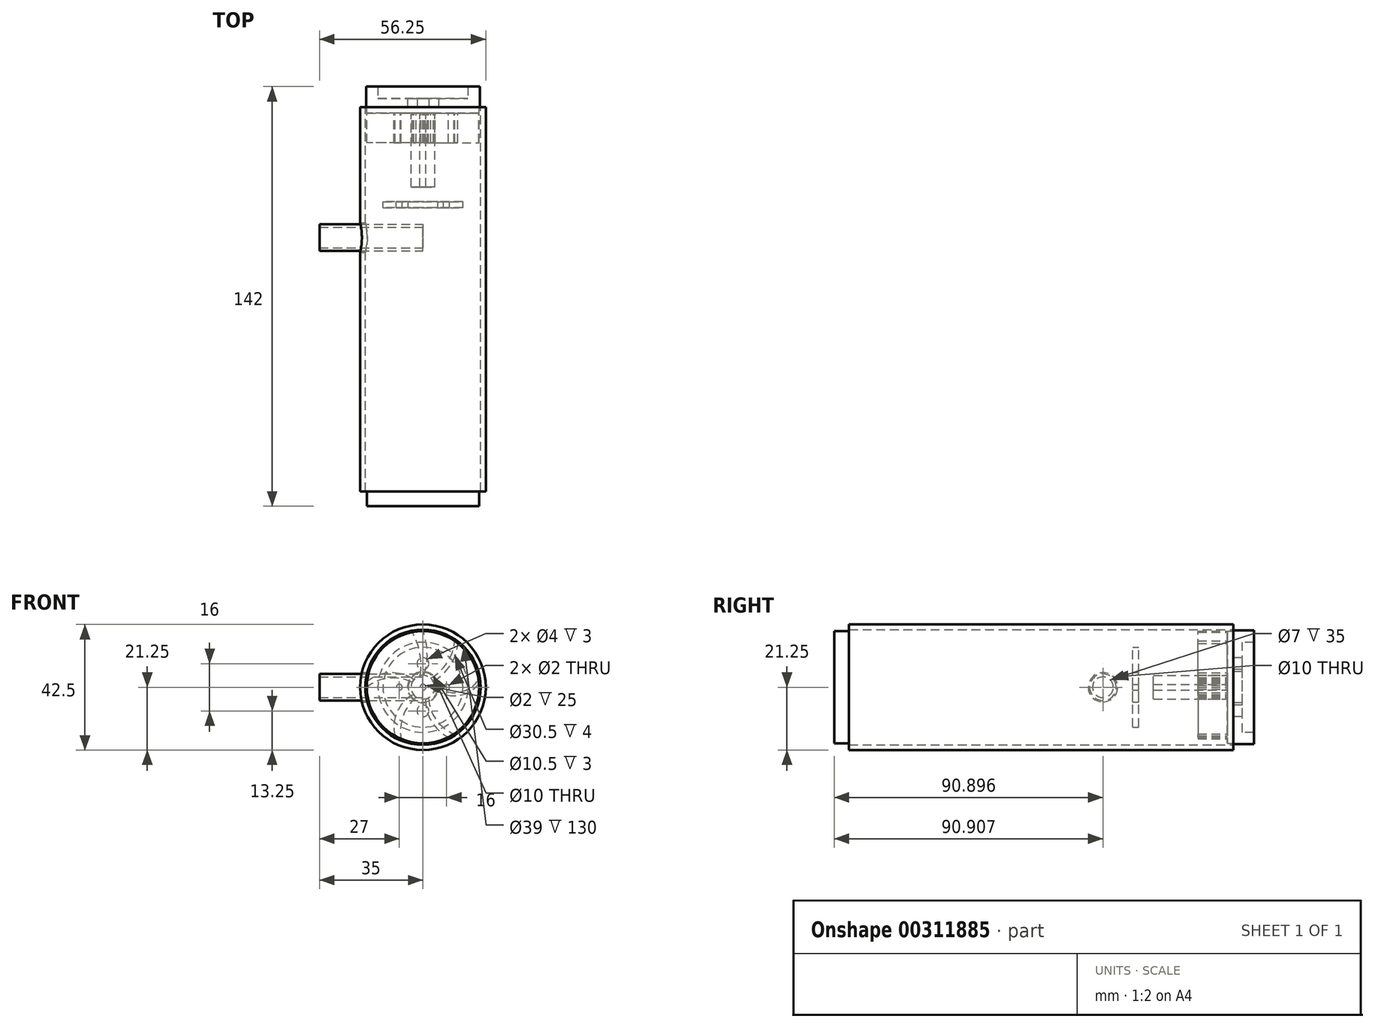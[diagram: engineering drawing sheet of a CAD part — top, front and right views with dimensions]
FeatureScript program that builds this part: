
annotation { "Feature Type Name" : "Feature", "Feature Type Description" : "" }
export const myFeature = defineFeature(function(context is Context, id is Id, definition is map)
    precondition{}
    {
        {
            var Q0;
            Q0=qCreatedBy(makeId("Front.planeOp"),FACE);
            var sketch = newSketch(context, id + "F0", { "sketchPlane" : qUnion([Q0])});
            skCircle(sketch, "E0", {"center": v(0, 0) * mm, "radius": 19.5 * mm});
            skCircle(sketch, "E1", {"center": v(0, 0) * mm, "radius": 21.25 * mm});
            skSolve(sketch);
        }
        {
            var Q0;
            Q0 = qSketchRegion(id + "F0", true);
            extrude(context, id + "F1", {"entities" : qUnion([Q0]), "depth" : 130 * mm});
        }
        {
            var Q0;
            Q0=qCreatedBy(makeId("Front.planeOp"),FACE);
            var sketch = newSketch(context, id + "F2", { "sketchPlane" : qUnion([Q0])});
            skCircle(sketch, "E2", {"center": v(0, 0) * mm, "radius": 19 * mm});
            skSolve(sketch);
        }
        {
            var Q0;
            Q0 = qSketchRegion(id + "F2", true);
            extrude(context, id + "F3", {"entities" : qUnion([Q0]), "depth" : 2 * mm});
        }
        {
            var Q0;
            Q0=makeQuery(id+"F3.opExtrude","CAP_FACE",FACE,{"disambiguationData":[OSD([sQuery(id+"F2.wireOp",EDGE,"E2")])],"isStart":false});
            var sketch = newSketch(context, id + "F4", { "sketchPlane" : qUnion([Q0])});
            skCircle(sketch, "E3", {"center": v(0, 0) * mm, "radius": 4.1 * mm});
            skArc(sketch, "E4", {"start": v(4.04, -0.63) * mm, "mid": v(11.9, -2.82) * mm, "end": v(18.96, 1.28) * mm});
            skArc(sketch, "E5", {"start": v(4.04, 0.63) * mm, "mid": v(11.86, -1.73) * mm, "end": v(18.83, 2.51) * mm});
            skArc(sketch, "E6", {"start": v(1.89, -3.63) * mm, "mid": v(4.47, -10.95) * mm, "end": v(10.5, -15.83) * mm});
            skArc(sketch, "E7", {"start": v(0.8, -4.02) * mm, "mid": v(2.9, -11.58) * mm, "end": v(8.66, -16.91) * mm});
            skArc(sketch, "E8", {"start": v(-3.11, 2.66) * mm, "mid": v(-11.15, 4.86) * mm, "end": v(-18.91, 1.83) * mm});
            skArc(sketch, "E9", {"start": v(-3.72, 1.7) * mm, "mid": v(-11.61, 3.1) * mm, "end": v(-19, 0) * mm});
            skArc(sketch, "E10", {"start": v(-3.24, -2.5) * mm, "mid": v(-8.8, -8.4) * mm, "end": v(-9.46, -16.48) * mm});
            skArc(sketch, "E11", {"start": v(-2.29, -3.4) * mm, "mid": v(-6.72, -9.76) * mm, "end": v(-7.43, -17.49) * mm});
            skArc(sketch, "E12", {"start": v(-0.88, 4) * mm, "mid": v(-1.03, 11.55) * mm, "end": v(-3.62, 18.65) * mm});
            skArc(sketch, "E13", {"start": v(0.36, 4.08) * mm, "mid": v(1.43, 11.57) * mm, "end": v(0, 19) * mm});
            skArc(sketch, "E14", {"start": v(2.63, 3.14) * mm, "mid": v(8.26, 8.38) * mm, "end": v(10.76, 15.66) * mm});
            skArc(sketch, "E15", {"start": v(3.5, 2.11) * mm, "mid": v(9.3, 7.43) * mm, "end": v(11.84, 14.86) * mm});
            skCircle(sketch, "E16", {"center": v(0, 0) * mm, "radius": 1 * mm});
            skSolve(sketch);
        }
        {
            var Q0;
            {var subQ0=sQuery(id+"F4.wireOp",EDGE,"E12");Q0=makeQuery(id+"F4.imprint","IMPRINT",FACE,{"disambiguationData":[TD([[makeQuery(id+"F4.imprint","IMPRINT",EDGE,{"derivedFrom":subQ0}),-1.0]])]});}
            var Q1;
            {var subQ0=sQuery(id+"F4.wireOp",EDGE,"E4");Q1=makeQuery(id+"F4.imprint","IMPRINT",FACE,{"disambiguationData":[TD([[makeQuery(id+"F4.imprint","IMPRINT",EDGE,{"derivedFrom":subQ0}),1.0]])]});}
            var Q2;
            {var subQ0=sQuery(id+"F4.wireOp",EDGE,"E6");Q2=makeQuery(id+"F4.imprint","IMPRINT",FACE,{"disambiguationData":[TD([[makeQuery(id+"F4.imprint","IMPRINT",EDGE,{"derivedFrom":subQ0}),-1.0]])]});}
            var Q3;
            {var subQ0=sQuery(id+"F4.wireOp",EDGE,"E10");Q3=makeQuery(id+"F4.imprint","IMPRINT",FACE,{"disambiguationData":[TD([[makeQuery(id+"F4.imprint","IMPRINT",EDGE,{"derivedFrom":subQ0}),1.0]])]});}
            var Q4;
            {var subQ0=sQuery(id+"F4.wireOp",EDGE,"E14");Q4=makeQuery(id+"F4.imprint","IMPRINT",FACE,{"disambiguationData":[TD([[makeQuery(id+"F4.imprint","IMPRINT",EDGE,{"derivedFrom":subQ0}),-1.0]])]});}
            var Q5;
            {var subQ0=sQuery(id+"F4.wireOp",EDGE,"E8");Q5=makeQuery(id+"F4.imprint","IMPRINT",FACE,{"disambiguationData":[TD([[makeQuery(id+"F4.imprint","IMPRINT",EDGE,{"derivedFrom":subQ0}),1.0]])]});}
            extrude(context, id + "F5", {"entities" : qUnion([Q0, Q1, Q2, Q3, Q4, Q5]), "operationType" : NewBodyOperationType.ADD, "depth" : 10 * mm});
        }
        {
            var Q0;
            {var subQ0=sQuery(id+"F4.wireOp",EDGE,"E8");var subQ1=makeQuery(id+"F3.opExtrude","CAP_EDGE",EDGE,{"disambiguationData":[OSD([sQuery(id+"F2.wireOp",EDGE,"E2")])],"isStart":false});var subQ2=makeQuery(id+"F4.imprint","INTERSECT",VERTEX,{"derivedFrom":[subQ1,subQ0]});Q0=makeQuery(id+"F4.imprint","IMPRINT",FACE,{"disambiguationData":[TD([[makeQuery(id+"F4.imprint","IMPRINT",EDGE,{"disambiguationData":[TD([[subQ2,1.0]])],"derivedFrom":subQ0}),-1.0]])]});}
            var sketch = newSketch(context, id + "F6", { "sketchPlane" : qUnion([Q0])});
            skCircle(sketch, "E17", {"center": v(0, 0) * mm, "radius": 4 * mm});
            skCircle(sketch, "E18", {"center": v(0, 0) * mm, "radius": 1 * mm});
            skSolve(sketch);
        }
        {
            var Q0;
            Q0 = qSketchRegion(id + "F6", true);
            extrude(context, id + "F7", {"entities" : qUnion([Q0]), "operationType" : NewBodyOperationType.ADD, "depth" : 25 * mm});
        }
        {
            var Q0;
            {var subQ0=sQuery(id+"F4.wireOp",EDGE,"E4");Q0=makeQuery(id+"F4.imprint","IMPRINT",FACE,{"disambiguationData":[TD([[makeQuery(id+"F4.imprint","IMPRINT",EDGE,{"derivedFrom":subQ0}),-1.0]])]});}
            cPlane(context, id + "F8", {"entities" : qUnion([Q0]), "cplaneType" : CPlaneType.OFFSET, "offset" : 30 * mm, "width" : 150 * mm, "height" : 150 * mm});
        }
        {
            var Q0;
            Q0=qCreatedBy(id+"F8.planeOp",FACE);
            var sketch = newSketch(context, id + "F9", { "sketchPlane" : qUnion([Q0])});
            skCircle(sketch, "E19", {"center": v(0, 0) * mm, "radius": 5 * mm});
            skCircle(sketch, "E20", {"center": v(0, 0) * mm, "radius": 13.5 * mm});
            skCircle(sketch, "E21", {"center": v(8, 0) * mm, "radius": 1 * mm});
            skCircle(sketch, "E22", {"center": v(-8, 0) * mm, "radius": 1 * mm});
            skSolve(sketch);
        }
        {
            var Q0;
            Q0=makeQuery(id+"F9.imprint","IMPRINT",FACE,{"disambiguationData":[TD([[makeQuery(id+"F9.imprint","IMPRINT",EDGE,{"derivedFrom":sQuery(id+"F9.wireOp",EDGE,"E19")}),-1.0]])]});
            extrude(context, id + "F10", {"entities" : qUnion([Q0]), "depth" : 2 * mm});
        }
        {
            var Q0;
            Q0=makeQuery(id+"F1.opExtrude","CAP_FACE",FACE,{"disambiguationData":[OSD([sQuery(id+"F0.wireOp",EDGE,"E0"),sQuery(id+"F0.wireOp",EDGE,"E1")])],"isStart":false});
            var sketch = newSketch(context, id + "F11", { "sketchPlane" : qUnion([Q0])});
            skCircle(sketch, "E23", {"center": v(0, 0) * mm, "radius": 19 * mm});
            skSolve(sketch);
        }
        {
            var Q0;
            Q0 = qSketchRegion(id + "F11", true);
            extrude(context, id + "F12", {"entities" : qUnion([Q0]), "depth" : 5 * mm});
        }
        {
            var Q0;
            Q0=qCreatedBy(makeId("Front.planeOp"),FACE);
            var sketch = newSketch(context, id + "F13", { "sketchPlane" : qUnion([Q0])});
            skCircle(sketch, "E24", {"center": v(0, 0) * mm, "radius": 19.25 * mm});
            skCircle(sketch, "E25", {"center": v(0, -8) * mm, "radius": 2 * mm});
            skCircle(sketch, "E26", {"center": v(0, 8) * mm, "radius": 2 * mm});
            skCircle(sketch, "E27", {"center": v(0, 0) * mm, "radius": 5.25 * mm});
            skSolve(sketch);
        }
        {
            var Q0;
            Q0=makeQuery(id+"F13.imprint","IMPRINT",FACE,{"disambiguationData":[TD([[makeQuery(id+"F13.imprint","IMPRINT",EDGE,{"derivedFrom":sQuery(id+"F13.wireOp",EDGE,"E24")}),1.0]])]});
            var sketch = newSketch(context, id + "F14", { "sketchPlane" : qUnion([Q0])});
            skCircle(sketch, "E28", {"center": v(0, 0) * mm, "radius": 19.25 * mm});
            skCircle(sketch, "E29", {"center": v(0, 0) * mm, "radius": 15.25 * mm});
            skSolve(sketch);
        }
        {
            var Q0;
            Q0 = qSketchRegion(id + "F14", true);
            extrude(context, id + "F15", {"entities" : qUnion([Q0]), "oppositeDirection" : true, "depth" : 7 * mm});
        }
        {
            var Q0;
            Q0 = qSketchRegion(id + "F13", true);
            extrude(context, id + "F16", {"entities" : qUnion([Q0]), "operationType" : NewBodyOperationType.ADD, "oppositeDirection" : true, "depth" : 3 * mm});
        }
        {
            var Q0;
            Q0=qCreatedBy(makeId("Right.planeOp"),FACE);
            var sketch = newSketch(context, id + "F17", { "sketchPlane" : qUnion([Q0])});
            skLineSegment(sketch, "E30", {"start": v(-69.18, 0) * mm, "end": v(0, 0) * mm, "construction": true});
            skCircle(sketch, "E31", {"center": v(-44.1, 0) * mm, "radius": 5 * mm});
            skSolve(sketch);
        }
        {
            var Q0;
            Q0 = qSketchRegion(id + "F17", true);
            extrude(context, id + "F18", {"entities" : qUnion([Q0]), "operationType" : NewBodyOperationType.REMOVE, "oppositeDirection" : true, "depth" : 25 * mm});
        }
        {
            var Q0;
            Q0=qCreatedBy(makeId("Right.planeOp"),FACE);
            var sketch = newSketch(context, id + "F19", { "sketchPlane" : qUnion([Q0])});
            skCircle(sketch, "E32", {"center": v(-44.1, 0) * mm, "radius": 4.5 * mm});
            skCircle(sketch, "E33", {"center": v(-44.1, 0) * mm, "radius": 3.5 * mm});
            skSolve(sketch);
        }
        {
            var Q0;
            Q0 = qSketchRegion(id + "F19", true);
            extrude(context, id + "F20", {"entities" : qUnion([Q0]), "operationType" : NewBodyOperationType.ADD, "oppositeDirection" : true, "depth" : 35 * mm});
        }
    });
